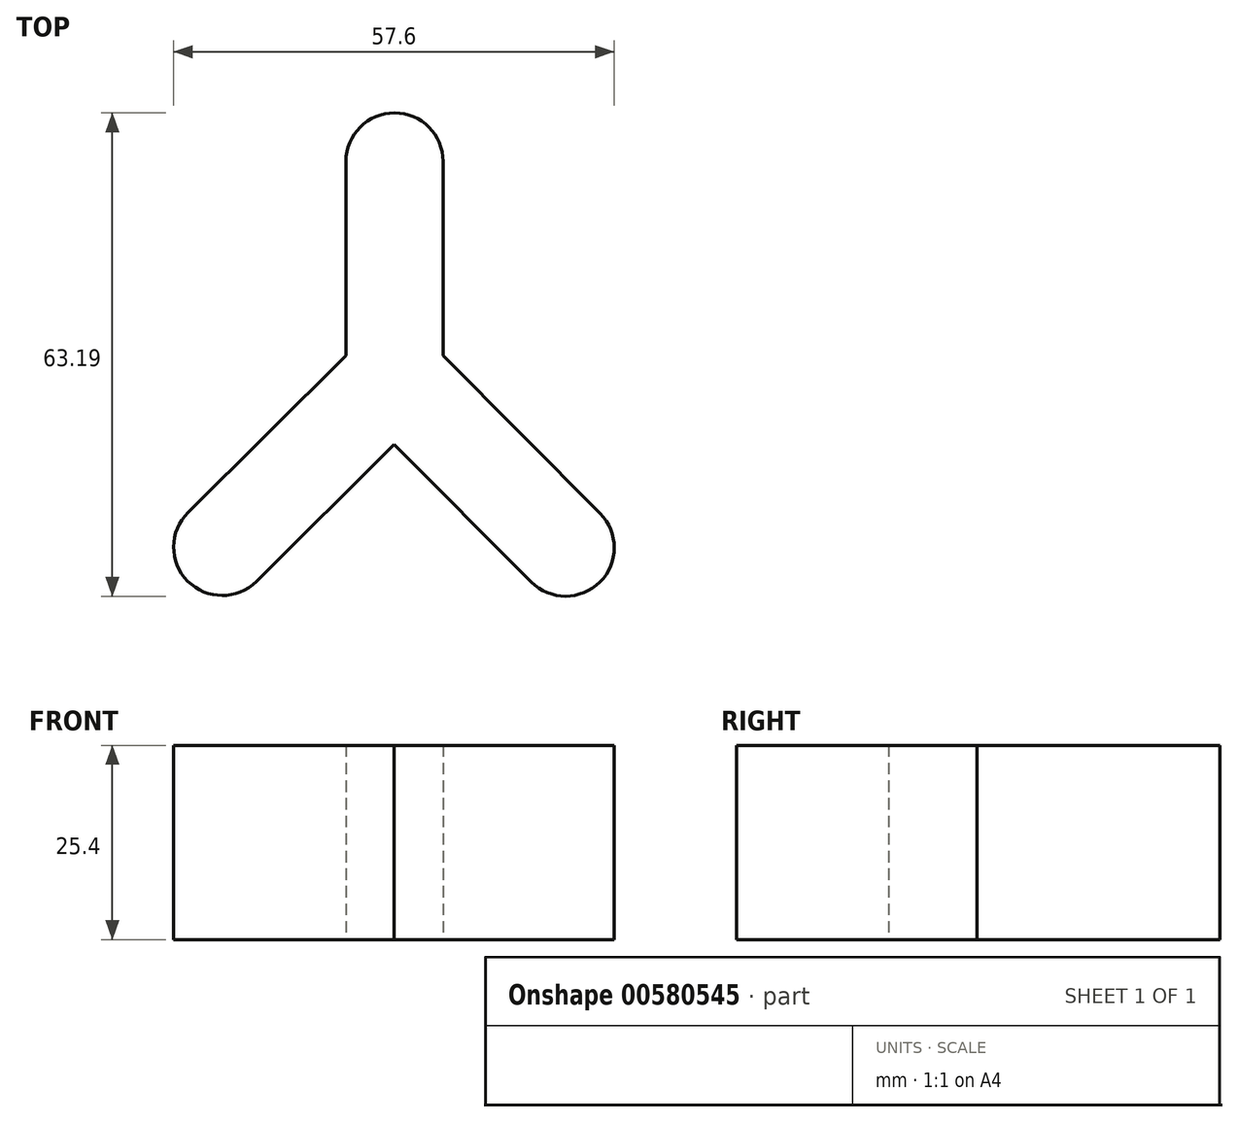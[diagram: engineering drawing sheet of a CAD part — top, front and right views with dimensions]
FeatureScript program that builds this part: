
annotation { "Feature Type Name" : "Feature", "Feature Type Description" : "" }
export const myFeature = defineFeature(function(context is Context, id is Id, definition is map)
    precondition{}
    {
        {
            var Q0;
            Q0=qCreatedBy(makeId("Top.planeOp"),FACE);
            var sketch = newSketch(context, id + "F0", { "sketchPlane" : qUnion([Q0])});
            skLineSegment(sketch, "E0", {"start": v(-25.48, 0) * mm, "end": v(-25.48, 25.4) * mm});
            skLineSegment(sketch, "E1", {"start": v(-25.48, 25.4) * mm, "end": v(-12.78, 25.4) * mm});
            skLineSegment(sketch, "E2", {"start": v(-12.78, 25.4) * mm, "end": v(-12.78, 0) * mm});
            skLineSegment(sketch, "E3", {"start": v(-12.78, 0) * mm, "end": v(7.74, -20.61) * mm});
            skLineSegment(sketch, "E4", {"start": v(7.74, -20.61) * mm, "end": v(-1.26, -29.57) * mm});
            skLineSegment(sketch, "E5", {"start": v(-1.26, -29.57) * mm, "end": v(-19.18, -11.57) * mm});
            skLineSegment(sketch, "E6", {"start": v(-19.18, -11.57) * mm, "end": v(-37.18, -29.49) * mm});
            skLineSegment(sketch, "E7", {"start": v(-37.18, -29.49) * mm, "end": v(-46.14, -20.49) * mm});
            skLineSegment(sketch, "E8", {"start": v(-46.14, -20.49) * mm, "end": v(-25.48, 0) * mm});
            skSolve(sketch);
        }
        {
            var Q0;
            Q0=makeQuery(id+"F0.imprint","IMPRINT",FACE,{"disambiguationData":[TD([[makeQuery(id+"F0.imprint","IMPRINT",EDGE,{"derivedFrom":sQuery(id+"F0.wireOp",EDGE,"E0")}),-1.0]])]});
            extrude(context, id + "F1", {"entities" : qUnion([Q0]), "depth" : 25.4 * mm, "offsetDistance" : 25.4 * mm});
        }
        {
            var Q0;
            Q0=makeQuery(id+"F1.opExtrude","CAP_FACE",FACE,{"disambiguationData":[OSD([sQuery(id+"F0.wireOp",EDGE,"E0"),sQuery(id+"F0.wireOp",EDGE,"E1"),sQuery(id+"F0.wireOp",EDGE,"E2"),sQuery(id+"F0.wireOp",EDGE,"E3"),sQuery(id+"F0.wireOp",EDGE,"E4"),sQuery(id+"F0.wireOp",EDGE,"E5"),sQuery(id+"F0.wireOp",EDGE,"E6"),sQuery(id+"F0.wireOp",EDGE,"E7"),sQuery(id+"F0.wireOp",EDGE,"E8")])],"isStart":false});
            var sketch = newSketch(context, id + "F2", { "sketchPlane" : qUnion([Q0])});
            skArc(sketch, "E9", {"start": v(-1.26, -29.57) * mm, "mid": v(7.72, -29.6) * mm, "end": v(7.74, -20.61) * mm});
            skArc(sketch, "E10", {"start": v(-46.14, -20.49) * mm, "mid": v(-46.16, -29.47) * mm, "end": v(-37.18, -29.49) * mm});
            skArc(sketch, "E11", {"start": v(-12.78, 25.4) * mm, "mid": v(-19.13, 31.75) * mm, "end": v(-25.48, 25.4) * mm});
            skSolve(sketch);
        }
        {
            var Q0;
            Q0=makeQuery(id+"F2.imprint","IMPRINT",FACE,{"disambiguationData":[TD([[makeQuery(id+"F2.imprint","IMPRINT",EDGE,{"derivedFrom":sQuery(id+"F2.wireOp",EDGE,"E11")}),1.0]])]});
            var Q1;
            Q1=makeQuery(id+"F2.imprint","IMPRINT",FACE,{"disambiguationData":[TD([[makeQuery(id+"F2.imprint","IMPRINT",EDGE,{"derivedFrom":sQuery(id+"F2.wireOp",EDGE,"E9")}),1.0]])]});
            var Q2;
            Q2=makeQuery(id+"F2.imprint","IMPRINT",FACE,{"disambiguationData":[TD([[makeQuery(id+"F2.imprint","IMPRINT",EDGE,{"derivedFrom":sQuery(id+"F2.wireOp",EDGE,"E10")}),1.0]])]});
            extrude(context, id + "F3", {"entities" : qUnion([Q0, Q1, Q2]), "operationType" : NewBodyOperationType.ADD, "oppositeDirection" : true, "depth" : 25.4 * mm, "offsetDistance" : 25.4 * mm});
        }
        {
            var Q0;
            {var subQ0=sQuery(id+"F0.wireOp",EDGE,"E1");var subQ1=sQuery(id+"F0.wireOp",EDGE,"E7");var subQ2=sQuery(id+"F0.wireOp",EDGE,"E4");Q0=makeQuery(id+"F3.boolean.opBoolean","MERGE",FACE,{"derivedFrom":[makeQuery(id+"F1.opExtrude","CAP_FACE",FACE,{"disambiguationData":[OSD([sQuery(id+"F0.wireOp",EDGE,"E0"),subQ0,sQuery(id+"F0.wireOp",EDGE,"E2"),sQuery(id+"F0.wireOp",EDGE,"E3"),subQ2,sQuery(id+"F0.wireOp",EDGE,"E5"),sQuery(id+"F0.wireOp",EDGE,"E6"),subQ1,sQuery(id+"F0.wireOp",EDGE,"E8")])],"isStart":false}),makeQuery(id+"F3.opExtrude","CAP_FACE",FACE,{"disambiguationData":[OSD([subQ2,sQuery(id+"F2.wireOp",EDGE,"E9")])],"isStart":true}),makeQuery(id+"F3.opExtrude","CAP_FACE",FACE,{"disambiguationData":[OSD([subQ1,sQuery(id+"F2.wireOp",EDGE,"E10")])],"isStart":true}),makeQuery(id+"F3.opExtrude","CAP_FACE",FACE,{"disambiguationData":[OSD([subQ0,sQuery(id+"F2.wireOp",EDGE,"E11")])],"isStart":true})]});}
            var sketch = newSketch(context, id + "F4", { "sketchPlane" : qUnion([Q0])});
            skCircle(sketch, "E12", {"center": v(-37.16, -20.42) * mm, "radius": 6.41 * mm});
            skCircle(sketch, "E13", {"center": v(-2.52, -18.6) * mm, "radius": 5.86 * mm});
            skPoint(sketch, "E13.centerSnap0", {"position": v(-2.52, -10.3) * mm});
            skSolve(sketch);
        }
        {
            var Q0;
            {var subQ0=sQuery(id+"F4.wireOp",EDGE,"E12");var subQ1=makeQuery(id+"F1.opExtrude","CAP_EDGE",EDGE,{"disambiguationData":[OSD([sQuery(id+"F0.wireOp",EDGE,"E8")])],"isStart":false});var subQ2=makeQuery(id+"F4.imprint","INTERSECT",VERTEX,{"disambiguationData":[OD(0.0)],"derivedFrom":[subQ1,subQ0]});Q0=makeQuery(id+"F4.imprint","IMPRINT",FACE,{"disambiguationData":[TD([[makeQuery(id+"F4.imprint","IMPRINT",EDGE,{"disambiguationData":[TD([[subQ2,1.0]])],"derivedFrom":subQ0}),1.0]])]});}
            var Q1;
            {var subQ0=sQuery(id+"F4.wireOp",EDGE,"E12");var subQ1=makeQuery(id+"F1.opExtrude","CAP_EDGE",EDGE,{"disambiguationData":[OSD([sQuery(id+"F0.wireOp",EDGE,"E8")])],"isStart":false});var subQ2=makeQuery(id+"F4.imprint","INTERSECT",VERTEX,{"disambiguationData":[OD(0.0)],"derivedFrom":[subQ1,subQ0]});Q1=makeQuery(id+"F4.imprint","IMPRINT",FACE,{"disambiguationData":[TD([[makeQuery(id+"F4.imprint","IMPRINT",EDGE,{"disambiguationData":[TD([[subQ2,-1.0]])],"derivedFrom":subQ0}),1.0]])]});}
            var Q2;
            Q2=makeQuery(id+"F4.imprint","IMPRINT",FACE,{"disambiguationData":[TD([[makeQuery(id+"F4.imprint","IMPRINT",EDGE,{"derivedFrom":sQuery(id+"F4.wireOp",EDGE,"E13")}),1.0]])]});
            extrude(context, id + "F5", {"entities" : qUnion([Q0, Q1, Q2]), "operationType" : NewBodyOperationType.REMOVE, "endBound" : BoundingType.THROUGH_ALL, "depth" : 25.4 * mm, "offsetDistance" : 25.4 * mm});
        }
    });
